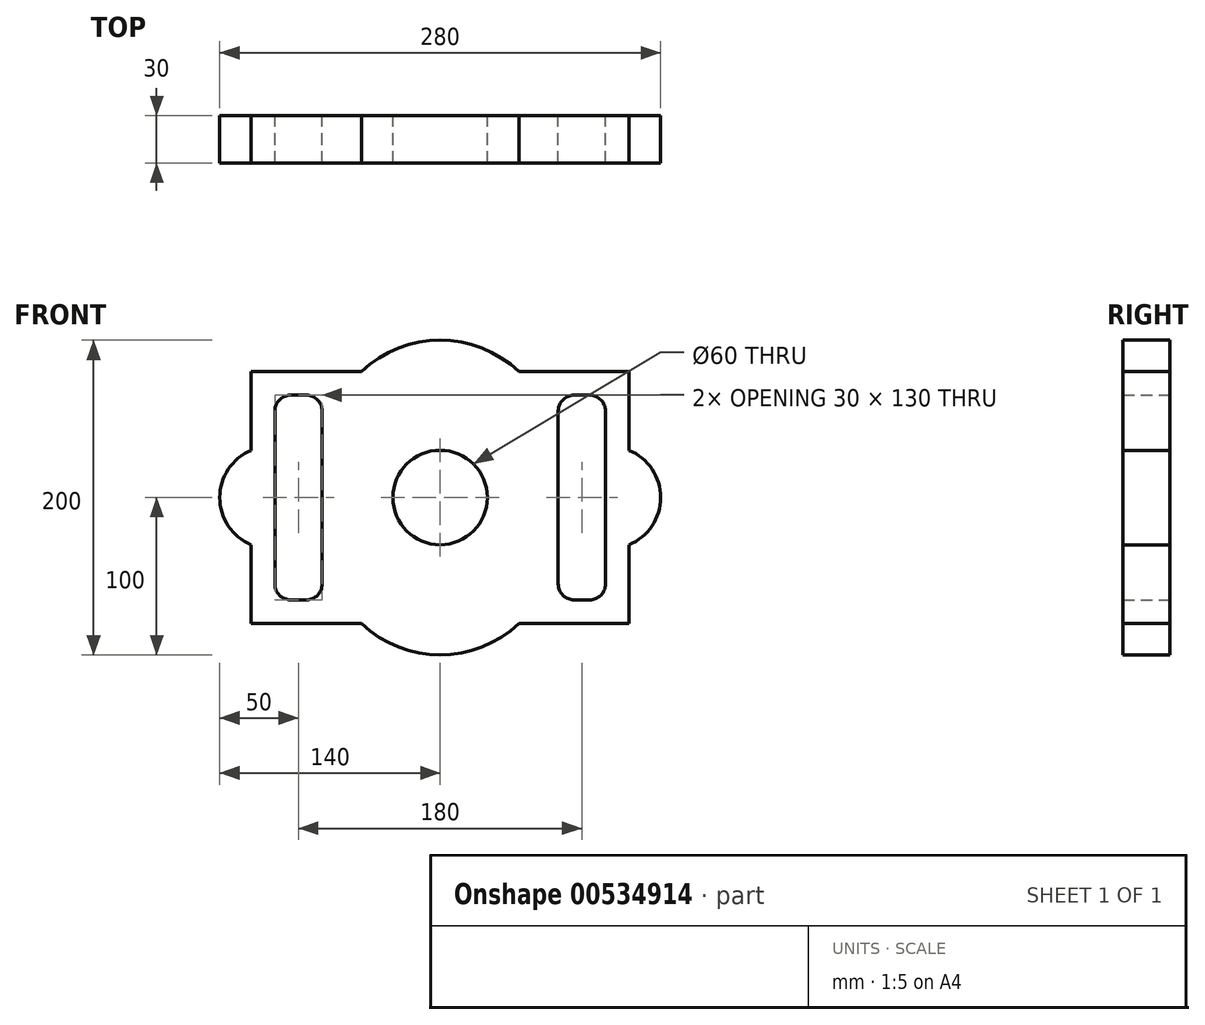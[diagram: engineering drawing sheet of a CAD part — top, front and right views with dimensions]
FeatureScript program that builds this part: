
annotation { "Feature Type Name" : "Feature", "Feature Type Description" : "" }
export const myFeature = defineFeature(function(context is Context, id is Id, definition is map)
    precondition{}
    {
        {
            var Q0;
            Q0=qCreatedBy(makeId("Front.planeOp"),FACE);
            var sketch = newSketch(context, id + "F0", { "sketchPlane" : qUnion([Q0])});
            skCircle(sketch, "E0", {"center": v(0, 0) * mm, "radius": 30 * mm});
            skLineSegment(sketch, "E1", {"start": v(-120, 80) * mm, "end": v(-50, 80) * mm});
            skLineSegment(sketch, "E2", {"start": v(50, 80) * mm, "end": v(120, 80) * mm});
            skArc(sketch, "E3", {"start": v(50, 80) * mm, "mid": v(0, 100) * mm, "end": v(-50, 80) * mm});
            skLineSegment(sketch, "E4", {"start": v(0, 0) * mm, "end": v(0, 27.5) * mm, "construction": true});
            skLineSegment(sketch, "E5", {"start": v(-120, 80) * mm, "end": v(-120, 30) * mm});
            skLineSegment(sketch, "E6", {"start": v(-120, -30) * mm, "end": v(-120, -80) * mm});
            skLineSegment(sketch, "E7", {"start": v(-120, -80) * mm, "end": v(-50, -80) * mm});
            skLineSegment(sketch, "E8", {"start": v(120, 80) * mm, "end": v(120, 30) * mm});
            skLineSegment(sketch, "E9", {"start": v(120, -30) * mm, "end": v(120, -80) * mm});
            skArc(sketch, "E10", {"start": v(-120, 30) * mm, "mid": v(-140, 0) * mm, "end": v(-120, -30) * mm});
            skArc(sketch, "E11", {"start": v(120, -30) * mm, "mid": v(140, 0) * mm, "end": v(120, 30) * mm});
            skPoint(sketch, "E12", {"position": v(140, 0) * mm});
            skPoint(sketch, "E13", {"position": v(-140, 0) * mm});
            skPoint(sketch, "E13.positionSnap0", {"position": v(-140, 0) * mm});
            skPoint(sketch, "E14", {"position": v(0, 100) * mm});
            skLineSegment(sketch, "E15", {"start": v(120, -80) * mm, "end": v(50, -80) * mm});
            skArc(sketch, "E16", {"start": v(-50, -80) * mm, "mid": v(0, -100) * mm, "end": v(50, -80) * mm});
            skLineSegment(sketch, "E17.bottom", {"start": v(-95, 65) * mm, "end": v(-85, 65) * mm});
            skLineSegment(sketch, "E17.top", {"start": v(-95, -65) * mm, "end": v(-85, -65) * mm});
            skLineSegment(sketch, "E17.left", {"start": v(-105, 55) * mm, "end": v(-105, -55) * mm});
            skLineSegment(sketch, "E17.right", {"start": v(-75, 55) * mm, "end": v(-75, -55) * mm});
            skLineSegment(sketch, "E18.bottom", {"start": v(95, -65) * mm, "end": v(85, -65) * mm});
            skLineSegment(sketch, "E18.top", {"start": v(95, 65) * mm, "end": v(85, 65) * mm});
            skLineSegment(sketch, "E18.left", {"start": v(105, -55) * mm, "end": v(105, 55) * mm});
            skLineSegment(sketch, "E18.right", {"start": v(75, -55) * mm, "end": v(75, 55) * mm});
            skLineSegment(sketch, "E19", {"start": v(-140, 0) * mm, "end": v(-105, 0) * mm, "construction": true});
            skPoint(sketch, "E20.visualSharp", {"position": v(-105, 65) * mm});
            skArc(sketch, "E20.filletArc", {"start": v(-95, 65) * mm, "mid": v(-102.07, 62.07) * mm, "end": v(-105, 55) * mm});
            skPoint(sketch, "E21.visualSharp", {"position": v(-75, 65) * mm});
            skArc(sketch, "E21.filletArc", {"start": v(-75, 55) * mm, "mid": v(-77.93, 62.07) * mm, "end": v(-85, 65) * mm});
            skPoint(sketch, "E22.visualSharp", {"position": v(-75, -65) * mm});
            skArc(sketch, "E22.filletArc", {"start": v(-85, -65) * mm, "mid": v(-77.93, -62.07) * mm, "end": v(-75, -55) * mm});
            skPoint(sketch, "E23.visualSharp", {"position": v(-105, -65) * mm});
            skArc(sketch, "E23.filletArc", {"start": v(-105, -55) * mm, "mid": v(-102.07, -62.07) * mm, "end": v(-95, -65) * mm});
            skPoint(sketch, "E24.visualSharp", {"position": v(75, -65) * mm});
            skArc(sketch, "E24.filletArc", {"start": v(75, -55) * mm, "mid": v(77.93, -62.07) * mm, "end": v(85, -65) * mm});
            skPoint(sketch, "E25.visualSharp", {"position": v(105, -65) * mm});
            skArc(sketch, "E25.filletArc", {"start": v(95, -65) * mm, "mid": v(102.07, -62.07) * mm, "end": v(105, -55) * mm});
            skPoint(sketch, "E26.visualSharp", {"position": v(75, 65) * mm});
            skArc(sketch, "E26.filletArc", {"start": v(85, 65) * mm, "mid": v(77.93, 62.07) * mm, "end": v(75, 55) * mm});
            skPoint(sketch, "E27.visualSharp", {"position": v(105, 65) * mm});
            skArc(sketch, "E27.filletArc", {"start": v(105, 55) * mm, "mid": v(102.07, 62.07) * mm, "end": v(95, 65) * mm});
            skLineSegment(sketch, "E28", {"start": v(-140, 0) * mm, "end": v(0, 0) * mm, "construction": true});
            skSolve(sketch);
        }
        {
            var Q0;
            Q0 = qSketchRegion(id + "F0", true);
            extrude(context, id + "F1", {"entities" : qUnion([Q0]), "depth" : 30 * mm, "offsetDistance" : 25 * mm});
        }
    });
